# Revit family: Наружный блок VRF системы
name_source: partatom
category: Mechanical Equipment
revit_build: Autodesk Revit 2016 (Build: 20150506_1715(x64)
units: mm (PartAtom-declared; Revit-internal decimal feet)

## family parameters
Cut with Voids When Loaded = No
Host = Face
Part Type = Normal
Room Calculation Point = No
Round Connector Dimension = Use Diameter
Shared = No

## types (6) — shared parameters
Default Elevation = 1219.2 mm  [stored 4 ft]
Высота ножек = 40 mm  [stored 0.131234 ft]
Глубина = 370 mm  [stored 1.21391 ft]
Диаметр газовой трубы = 15.88 mm  [stored 0.0520997 ft]
Диаметр жидкостной трубы = 9.53 mm
Длина ножек = 400 mm  [stored 1.31234 ft]
Наименование = Наружный блок VRF-системы
Производитель = Electrolux
Расстояние между ножек = 660 mm
Таблица модель = Модель
Таблица наименование = Наименование
Таблица параметров = Таблица параметров
Таблица расход воздуха = Расход воздуха
Таблица тип хладагента = Тип хладагента
Таблица уровень звукового давления = Уровень звукового давления
Таблица электропитание = Электропитание
Тип хладогента = R410А
Фаза = 1
Частота сети = 50 Hz
Ширина = 950 mm  [stored 3.1168 ft]
Ширина ножек = 60 mm  [stored 0.19685 ft]
Эл. питание(коннектор) = 220 V
Электропитание, (В) = 220

## per-type parameters (varying)
| type | ESVMO-SF-80/100/125-M | SCOP, (кВт/кВт) | SEER, (кВт/кВт) | Артикул | Вес | Высота | Максимальная потребляемая мощность_Нагрев | Максимальная потребляемая мощность_Охлаждение | Максимальное кол-во подключаемых внутренних блоков, шт | Максимальный ток | Масса хладагента | Расход воздуха, (м.куб/ч) | Теплопроизводительность | Уровень звукового давления, (Дб(А)) | Холодопроизводительность | Эффективная потребляемая мощность_Нагрев | Эффективная потребляемая мощность_Охлаждение |
| ESVMO-SF-80-M | Yes | 8.2 | 7.2 | 1040284 | 65.00 kg | 800 mm  [stored 2.62467 ft] | 1.94 kW | 1.86 kW | 3 | 20 A | 2.50 kg | 2700 | 9.50 kW | 44-42-38 | 8.00 kW | 1.16 kW | 1.12 kW |
| ESVMO-SF-100-М | Yes | 7.7 | 7 | 1040285 | 73.00 kg | 800 mm  [stored 2.62467 ft] | 2.43 kW | 2.38 kW | 4 | 29 A | 2.80 kg | 4800 | 11.20 kW | 47-45-41 | 10.00 kW | 1.46 kW | 1.43 kW |
| ESVMO-SF-125-М | Yes | 7.7 | 7.1 | 1040286 | 78.00 kg | 800 mm  [stored 2.62467 ft] | 3.04 kW | 2.94 kW | 4 | 32 A | 2.80 kg | 5400 | 14.00 kW | 49-46-42 | 12.50 kW | 1.82 kW | 1.76 kW |
| ESVMO-SF-120 | No | 6.9 | 6.8 | 1022667 | 93.00 kg | 1380 mm  [stored 4.52756 ft] | 2.98 kW | 2.99 kW | 7 | 28 A | 4.00 kg | 5400 | 12.50 kW | 51-49-45 | 11.20 kW | 1.82 kW | 1.65 kW |
| ESVMO-SF-140 | No | 6.4 | 6 | 1022668 | 95.00 kg | 1380 mm  [stored 4.52756 ft] | 4.03 kW | 3.92 kW | 7 | 29 A | 4.00 kg | 5400 | 16.00 kW | 53-51-47 | 14.00 kW | 2.52 kW | 2.33 kW |
| ESVMO-SF-160 | No | 6.1 | 5.5 | 1022669 | 97.00 kg | 1380 mm  [stored 4.52756 ft] | 4.74 kW | 4.44 kW | 7 | 30 A | 4.00 kg | 6000 | 18.00 kW | 53-51-47 | 15.50 kW | 2.94 kW | 2.81 kW |

note: column(s) folded — value = type name in every type: Модель

type visibility flags (boolean, named after types; folded from table):
- ESVMO-SF-80-M: Yes: (none)
- ESVMO-SF-100-М: Yes: (none)
- ESVMO-SF-125-М: Yes: (none)
- ESVMO-SF-120: Yes: ESVMO-SF-120/140/160
- ESVMO-SF-140: Yes: ESVMO-SF-120/140/160
- ESVMO-SF-160: Yes: ESVMO-SF-120/140/160

note: [stored X ft] marks values corroborated as IEEE doubles in the binary element streams (Revit-internal decimal feet)
